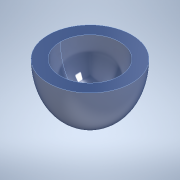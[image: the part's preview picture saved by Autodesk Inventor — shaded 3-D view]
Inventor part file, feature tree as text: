
AUTODESK INVENTOR PART (.ipt)
format: ipt  version: 2022 (Build 260153000, 153)  size: 258,560 bytes
history: native  units: in
note: dims shown in document units (in); Inventor stores cm internally (conversion verified against a paired STEP export)
features: revolve x1, thicken_offset x1, shell x1, sketch x1
ambient origin geometry x8: Origin, YZ Plane, XZ Plane, XY Plane, X Axis, Y Axis, Z Axis, Center Point
bodies: Body1 (feature_tree)
feature tree (4):
  revolve  "Revolution2"  [1 undecoded]
  thicken_offset  "Thicken2"
  shell  "Shell2"  Thickness=0.5in
  sketch  "Sketch5"  dims[d16=90.0deg d17=0.5in d18=1.0in d19=0.5in]
note: 1 required parameter value undecoded (feature->parameter linkage not recoverable at this tier; creation-order binding heuristic only, values carry confidence <= 0.55)
